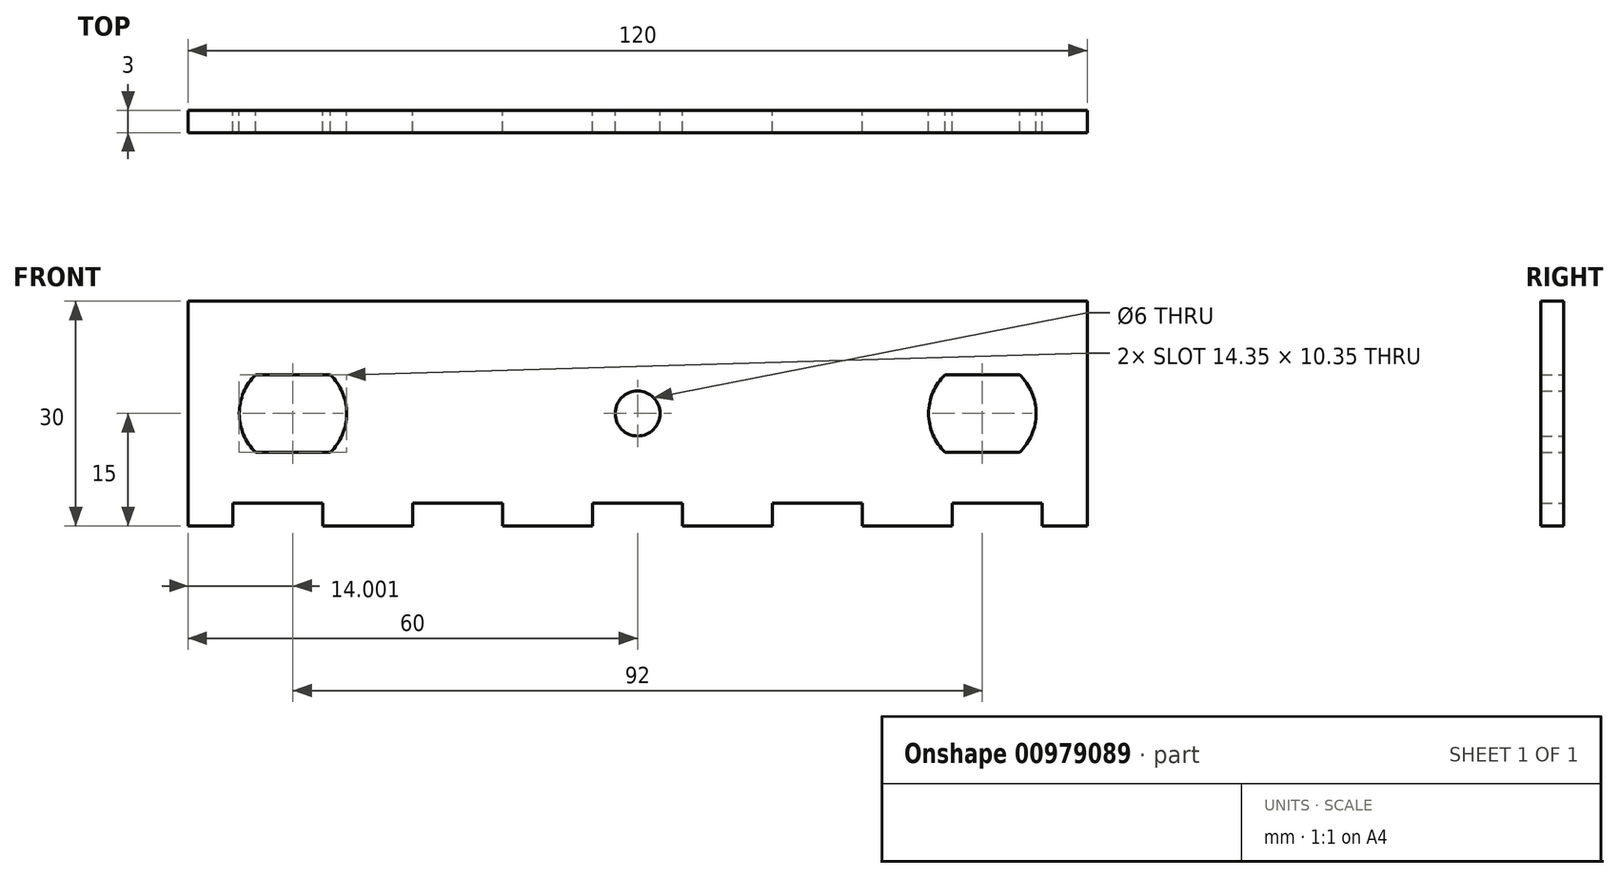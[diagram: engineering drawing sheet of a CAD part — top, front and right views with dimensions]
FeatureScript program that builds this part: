
annotation { "Feature Type Name" : "Feature", "Feature Type Description" : "" }
export const myFeature = defineFeature(function(context is Context, id is Id, definition is map)
    precondition{}
    {
        {
            var Q0;
            Q0=qCreatedBy(makeId("Front.planeOp"),FACE);
            var sketch = newSketch(context, id + "F0", { "sketchPlane" : qUnion([Q0])});
            skCircle(sketch, "E0", {"center": v(-46, 0) * mm, "radius": 7.17 * mm});
            skCircle(sketch, "E1", {"center": v(0, 0) * mm, "radius": 3 * mm});
            skLineSegment(sketch, "E2", {"start": v(-50.97, 5.17) * mm, "end": v(-41.03, 5.17) * mm});
            skLineSegment(sketch, "E3", {"start": v(-50.97, -5.17) * mm, "end": v(-41.03, -5.17) * mm});
            skCircle(sketch, "E4.MirrorC", {"center": v(46, 0) * mm, "radius": 7.17 * mm});
            skLineSegment(sketch, "E5.bottom", {"start": v(6, -12) * mm, "end": v(-6, -12) * mm});
            skLineSegment(sketch, "E5.left", {"start": v(6, -12) * mm, "end": v(6, -15) * mm});
            skLineSegment(sketch, "E5.right", {"start": v(-6, -12) * mm, "end": v(-6, -15) * mm});
            skLineSegment(sketch, "E6.1.0.0", {"start": v(30, -12) * mm, "end": v(30, -15) * mm});
            skLineSegment(sketch, "E6.1.0.1", {"start": v(18, -12) * mm, "end": v(18, -15) * mm});
            skLineSegment(sketch, "E6.1.0.2", {"start": v(30, -12) * mm, "end": v(18, -12) * mm});
            skLineSegment(sketch, "E6.2.0.0", {"start": v(54, -12) * mm, "end": v(54, -15) * mm});
            skLineSegment(sketch, "E6.2.0.1", {"start": v(42, -12) * mm, "end": v(42, -15) * mm});
            skLineSegment(sketch, "E6.2.0.2", {"start": v(54, -12) * mm, "end": v(42, -12) * mm});
            skLineSegment(sketch, "E7.1.0.0", {"start": v(-18, -12) * mm, "end": v(-30, -12) * mm});
            skLineSegment(sketch, "E7.1.0.1", {"start": v(-30, -12) * mm, "end": v(-30, -15) * mm});
            skLineSegment(sketch, "E7.1.0.3", {"start": v(-18, -12) * mm, "end": v(-18, -15) * mm});
            skLineSegment(sketch, "E7.2.0.0", {"start": v(-42, -12) * mm, "end": v(-54, -12) * mm});
            skLineSegment(sketch, "E7.2.0.1", {"start": v(-54, -12) * mm, "end": v(-54, -15) * mm});
            skLineSegment(sketch, "E7.2.0.3", {"start": v(-42, -12) * mm, "end": v(-42, -15) * mm});
            skLineSegment(sketch, "E7.direction1", {"start": v(-6, -15) * mm, "end": v(-30, -15) * mm, "construction": true});
            skLineSegment(sketch, "E8.bottom", {"start": v(60, 15) * mm, "end": v(-60, 15) * mm});
            skLineSegment(sketch, "E8.top", {"start": v(60, -15) * mm, "end": v(-60, -15) * mm});
            skLineSegment(sketch, "E8.left", {"start": v(60, 15) * mm, "end": v(60, -15) * mm});
            skLineSegment(sketch, "E8.right", {"start": v(-60, 15) * mm, "end": v(-60, -15) * mm});
            skLineSegment(sketch, "E9", {"start": v(41.03, -5.18) * mm, "end": v(50.97, -5.18) * mm});
            skLineSegment(sketch, "E10", {"start": v(46, 0) * mm, "end": v(43.17, 0) * mm});
            skLineSegment(sketch, "E11.MirrorCS", {"start": v(41.03, 5.17) * mm, "end": v(50.97, 5.17) * mm});
            skSolve(sketch);
        }
        {
            var Q0;
            Q0=makeQuery(id+"F0.imprint","IMPRINT",FACE,{"disambiguationData":[TD([[makeQuery(id+"F0.imprint","IMPRINT",EDGE,{"derivedFrom":sQuery(id+"F0.wireOp",EDGE,"E1")}),-1.0]])]});
            var Q1;
            {var subQ0=sQuery(id+"F0.wireOp",EDGE,"E11.MirrorCS");Q1=makeQuery(id+"F0.imprint","IMPRINT",FACE,{"disambiguationData":[TD([[makeQuery(id+"F0.imprint","IMPRINT",EDGE,{"derivedFrom":subQ0}),1.0]])]});}
            var Q2;
            {var subQ0=sQuery(id+"F0.wireOp",EDGE,"E9");Q2=makeQuery(id+"F0.imprint","IMPRINT",FACE,{"disambiguationData":[TD([[makeQuery(id+"F0.imprint","IMPRINT",EDGE,{"derivedFrom":subQ0}),-1.0]])]});}
            var Q3;
            {var subQ0=sQuery(id+"F0.wireOp",EDGE,"E2");Q3=makeQuery(id+"F0.imprint","IMPRINT",FACE,{"disambiguationData":[TD([[makeQuery(id+"F0.imprint","IMPRINT",EDGE,{"derivedFrom":subQ0}),1.0]])]});}
            var Q4;
            {var subQ0=sQuery(id+"F0.wireOp",EDGE,"E3");Q4=makeQuery(id+"F0.imprint","IMPRINT",FACE,{"disambiguationData":[TD([[makeQuery(id+"F0.imprint","IMPRINT",EDGE,{"derivedFrom":subQ0}),-1.0]])]});}
            extrude(context, id + "F1", {"entities" : qUnion([Q0, Q1, Q2, Q3, Q4]), "depth" : 3 * mm, "offsetDistance" : 25 * mm});
        }
    });
